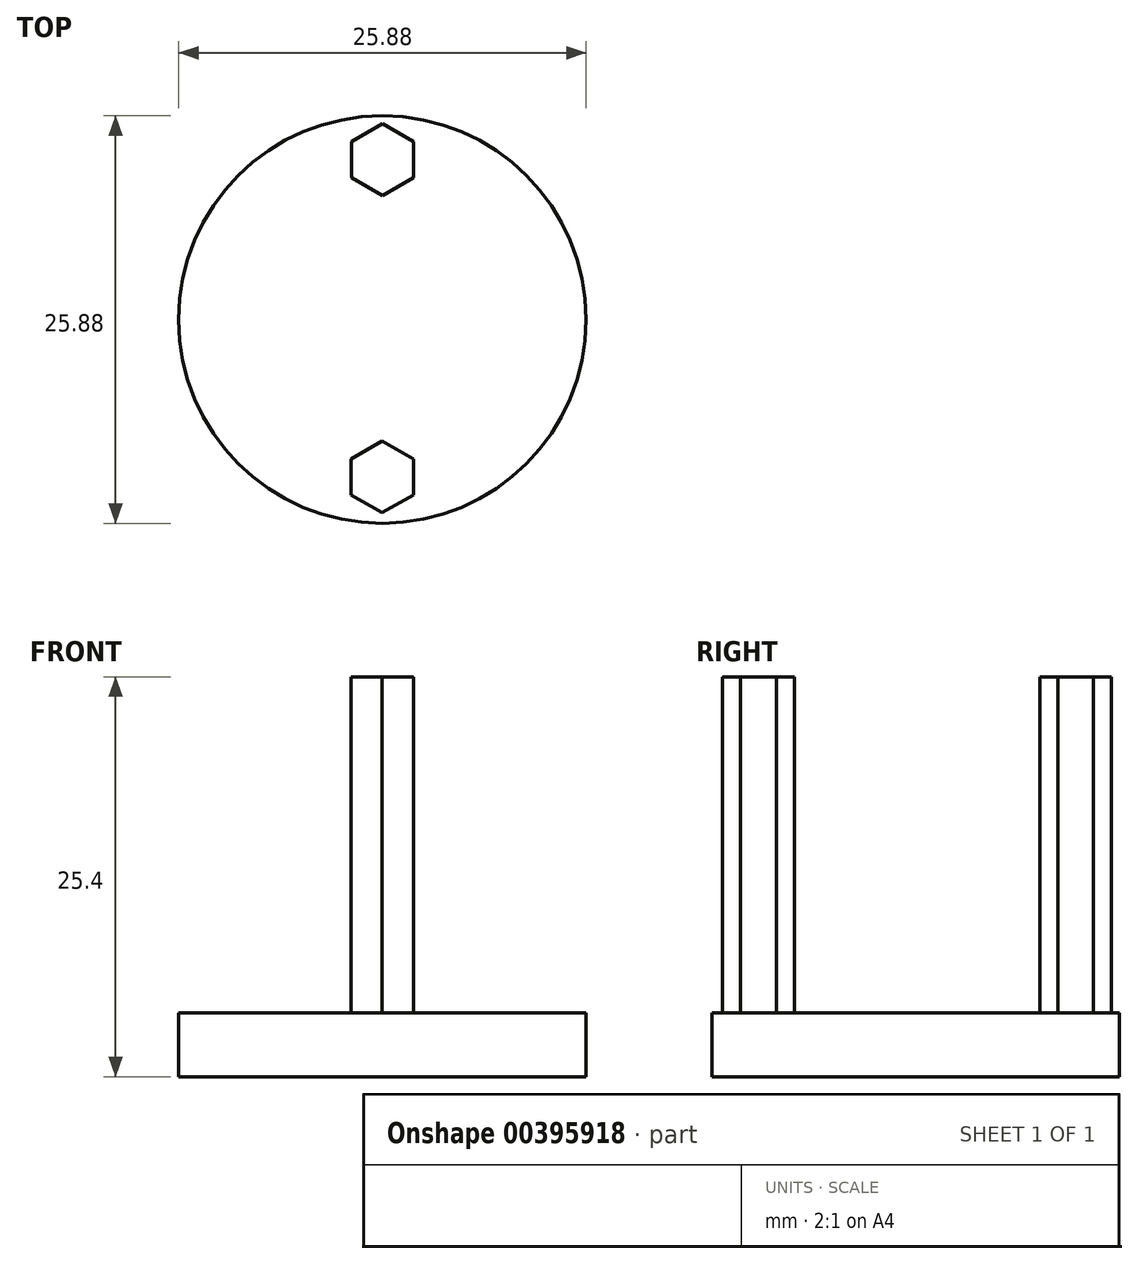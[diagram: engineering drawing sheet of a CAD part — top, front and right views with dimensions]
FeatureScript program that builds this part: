
annotation { "Feature Type Name" : "Feature", "Feature Type Description" : "" }
export const myFeature = defineFeature(function(context is Context, id is Id, definition is map)
    precondition{}
    {
        {
            var Q0;
            Q0=qCreatedBy(makeId("Top.planeOp"),FACE);
            var sketch = newSketch(context, id + "F0", { "sketchPlane" : qUnion([Q0])});
            skCircle(sketch, "E0", {"center": v(0, 0) * mm, "radius": 12.94 * mm});
            skSolve(sketch);
        }
        {
            var Q0;
            Q0=makeQuery(id+"F0.imprint","IMPRINT",FACE,{"disambiguationData":[TD([[makeQuery(id+"F0.imprint","IMPRINT",EDGE,{"derivedFrom":sQuery(id+"F0.wireOp",EDGE,"E0")}),1.0]])]});
            extrude(context, id + "F1", {"entities" : qUnion([Q0]), "depth" : 4.06 * mm});
        }
        {
            var Q0;
            Q0=qCreatedBy(makeId("Top.planeOp"),FACE);
            var sketch = newSketch(context, id + "F2", { "sketchPlane" : qUnion([Q0])});
            skCircle(sketch, "E1.cCircle", {"center": v(0, 10.16) * mm, "radius": 1.97 * mm, "construction": true});
            skLineSegment(sketch, "E1.0", {"start": v(1.98, 11.3) * mm, "end": v(1.98, 9.02) * mm});
            skLineSegment(sketch, "E1.1", {"start": v(1.98, 9.02) * mm, "end": v(0, 7.88) * mm});
            skLineSegment(sketch, "E1.2", {"start": v(0, 7.88) * mm, "end": v(-1.97, 9.02) * mm});
            skLineSegment(sketch, "E1.3", {"start": v(-1.97, 9.02) * mm, "end": v(-1.97, 11.3) * mm});
            skLineSegment(sketch, "E1.4", {"start": v(-1.97, 11.3) * mm, "end": v(0, 12.43) * mm});
            skLineSegment(sketch, "E1.5", {"start": v(0, 12.43) * mm, "end": v(1.98, 11.3) * mm});
            skPoint(sketch, "E1.0.midPoint", {"position": v(1.98, 10.16) * mm});
            skSolve(sketch);
        }
        {
            var Q0;
            Q0=makeQuery(id+"F2.imprint","IMPRINT",FACE,{"disambiguationData":[TD([[makeQuery(id+"F2.imprint","IMPRINT",EDGE,{"derivedFrom":sQuery(id+"F2.wireOp",EDGE,"E1.0")}),-1.0]])]});
            var sketch = newSketch(context, id + "F3", { "sketchPlane" : qUnion([Q0])});
            skCircle(sketch, "E2.cCircle", {"center": v(0, -10) * mm, "radius": 1.97 * mm, "construction": true});
            skLineSegment(sketch, "E2.0", {"start": v(1.96, -8.86) * mm, "end": v(1.96, -11.13) * mm});
            skLineSegment(sketch, "E2.1", {"start": v(1.96, -11.13) * mm, "end": v(0, -12.27) * mm});
            skLineSegment(sketch, "E2.2", {"start": v(0, -12.27) * mm, "end": v(-1.98, -11.13) * mm});
            skLineSegment(sketch, "E2.3", {"start": v(-1.98, -11.13) * mm, "end": v(-1.98, -8.86) * mm});
            skLineSegment(sketch, "E2.4", {"start": v(-1.98, -8.86) * mm, "end": v(0, -7.72) * mm});
            skLineSegment(sketch, "E2.5", {"start": v(0, -7.72) * mm, "end": v(1.96, -8.86) * mm});
            skSolve(sketch);
        }
        {
            var Q0;
            Q0=makeQuery(id+"F2.imprint","IMPRINT",FACE,{"disambiguationData":[TD([[makeQuery(id+"F2.imprint","IMPRINT",EDGE,{"derivedFrom":sQuery(id+"F2.wireOp",EDGE,"E1.0")}),-1.0]])]});
            extrude(context, id + "F4", {"entities" : qUnion([Q0]), "operationType" : NewBodyOperationType.ADD, "depth" : 25.4 * mm});
        }
        {
            var Q0;
            Q0=makeQuery(id+"F3.imprint","IMPRINT",FACE,{"disambiguationData":[TD([[makeQuery(id+"F3.imprint","IMPRINT",EDGE,{"derivedFrom":sQuery(id+"F3.wireOp",EDGE,"E2.0")}),-1.0]])]});
            extrude(context, id + "F5", {"entities" : qUnion([Q0]), "operationType" : NewBodyOperationType.ADD, "depth" : 25.4 * mm});
        }
    });
